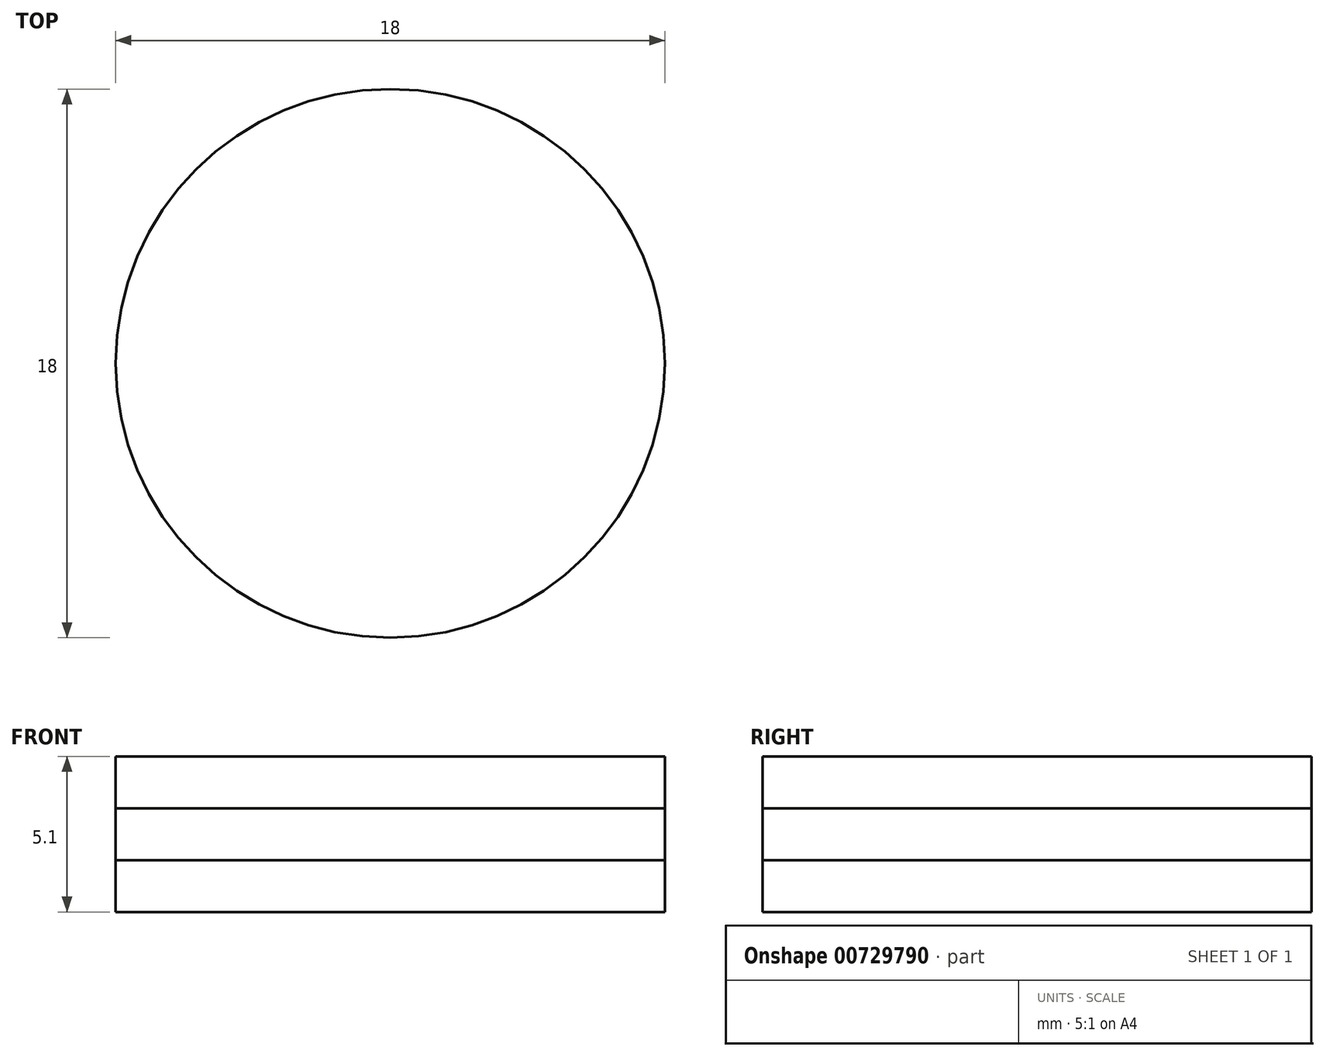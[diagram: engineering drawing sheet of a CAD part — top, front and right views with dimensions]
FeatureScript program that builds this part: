
annotation { "Feature Type Name" : "Feature", "Feature Type Description" : "" }
export const myFeature = defineFeature(function(context is Context, id is Id, definition is map)
    precondition{}
    {
        {
            var Q0;
            Q0=qCreatedBy(makeId("Top.planeOp"),FACE);
            var sketch = newSketch(context, id + "F0", { "sketchPlane" : qUnion([Q0])});
            skCircle(sketch, "E0", {"center": v(0, 0) * mm, "radius": 9 * mm});
            skSolve(sketch);
        }
        {
            var Q0;
            Q0=makeQuery(id+"F0.imprint","IMPRINT",FACE,{"disambiguationData":[TD([[makeQuery(id+"F0.imprint","IMPRINT",EDGE,{"derivedFrom":sQuery(id+"F0.wireOp",EDGE,"E0")}),1.0]])]});
            extrude(context, id + "F1", {"entities" : qUnion([Q0]), "endBound" : BoundingType.SYMMETRIC, "depth" : 1.7 * mm, "offsetDistance" : 25 * mm});
        }
        {
            var Q0;
            Q0=makeQuery(id+"F1.opExtrude","SWEPT_BODY",BODY,{"disambiguationData":[OSD([sQuery(id+"F0.wireOp",EDGE,"E0")])]});
            var Q1;
            Q1=makeQuery(id+"F1.opExtrude","CAP_FACE",FACE,{"disambiguationData":[OSD([sQuery(id+"F0.wireOp",EDGE,"E0")])],"isStart":false});
            mirror(context, id + "F2", {"entities" : qUnion([Q0]), "mirrorPlane" : qUnion([Q1])});
        }
        {
            var Q0;
            Q0=makeQuery(id+"F1.opExtrude","SWEPT_BODY",BODY,{"disambiguationData":[OSD([sQuery(id+"F0.wireOp",EDGE,"E0")])]});
            var Q1;
            Q1=makeQuery(id+"F1.opExtrude","CAP_FACE",FACE,{"disambiguationData":[OSD([sQuery(id+"F0.wireOp",EDGE,"E0")])],"isStart":true});
            mirror(context, id + "F3", {"entities" : qUnion([Q0]), "mirrorPlane" : qUnion([Q1])});
        }
    });
